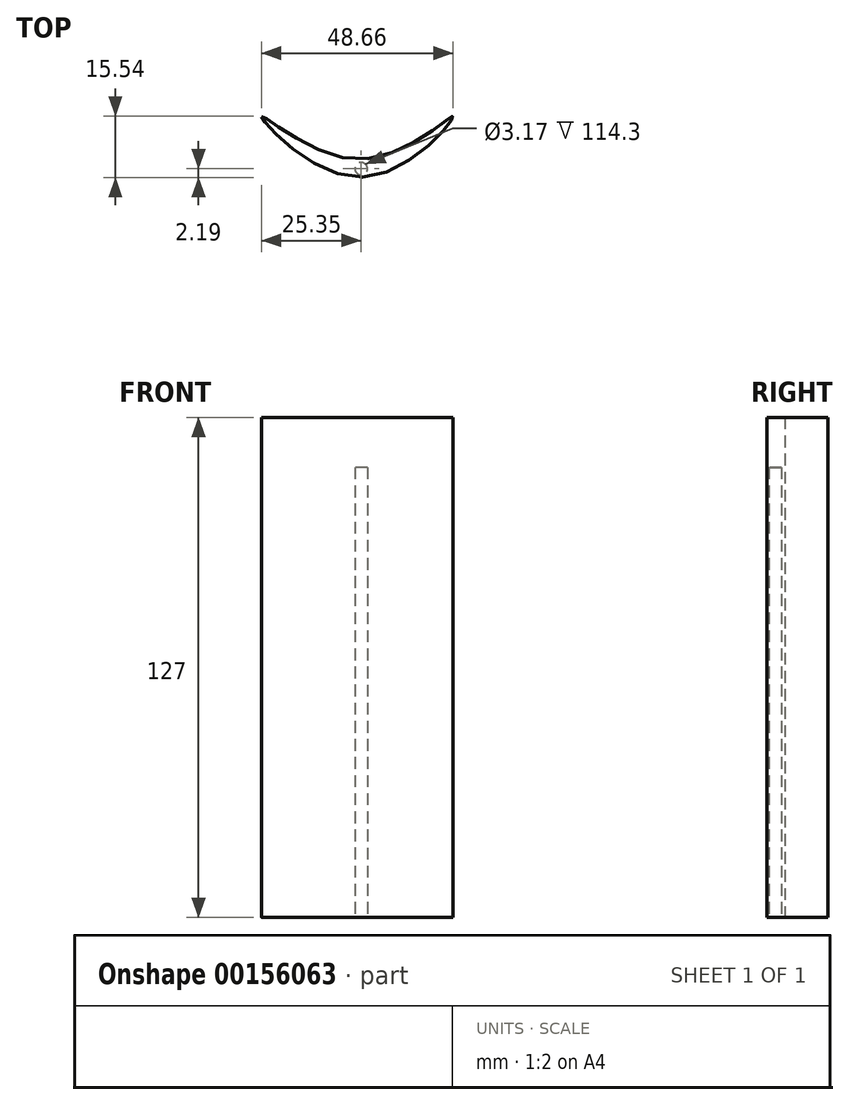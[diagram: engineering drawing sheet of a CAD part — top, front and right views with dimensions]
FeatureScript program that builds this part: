
annotation { "Feature Type Name" : "Feature", "Feature Type Description" : "" }
export const myFeature = defineFeature(function(context is Context, id is Id, definition is map)
    precondition{}
    {
        {
            var Q0;
            Q0=qCreatedBy(makeId("Top.planeOp"),FACE);
            var sketch = newSketch(context, id + "F0", { "sketchPlane" : qUnion([Q0])});
            skFitSpline(sketch, "E0", {"points": [v(-25.35, 0) * mm, v(0, -15.49) * mm, v(23.3, 0) * mm, v(0, -10.88) * mm, v(-25.35, 0) * mm]});
            skSolve(sketch);
        }
        {
            var Q0;
            Q0 = qSketchRegion(id + "F0", true);
            extrude(context, id + "F1", {"entities" : qUnion([Q0]), "depth" : 127 * mm});
        }
        {
            var Q0;
            Q0=qCreatedBy(makeId("Top.planeOp"),FACE);
            var sketch = newSketch(context, id + "F2", { "sketchPlane" : qUnion([Q0])});
            skCircle(sketch, "E1", {"center": v(0, -13.3) * mm, "radius": 1.59 * mm});
            skSolve(sketch);
        }
        {
            var Q0;
            Q0 = qSketchRegion(id + "F2", true);
            extrude(context, id + "F3", {"entities" : qUnion([Q0]), "operationType" : NewBodyOperationType.REMOVE, "depth" : 114.3 * mm});
        }
    });
